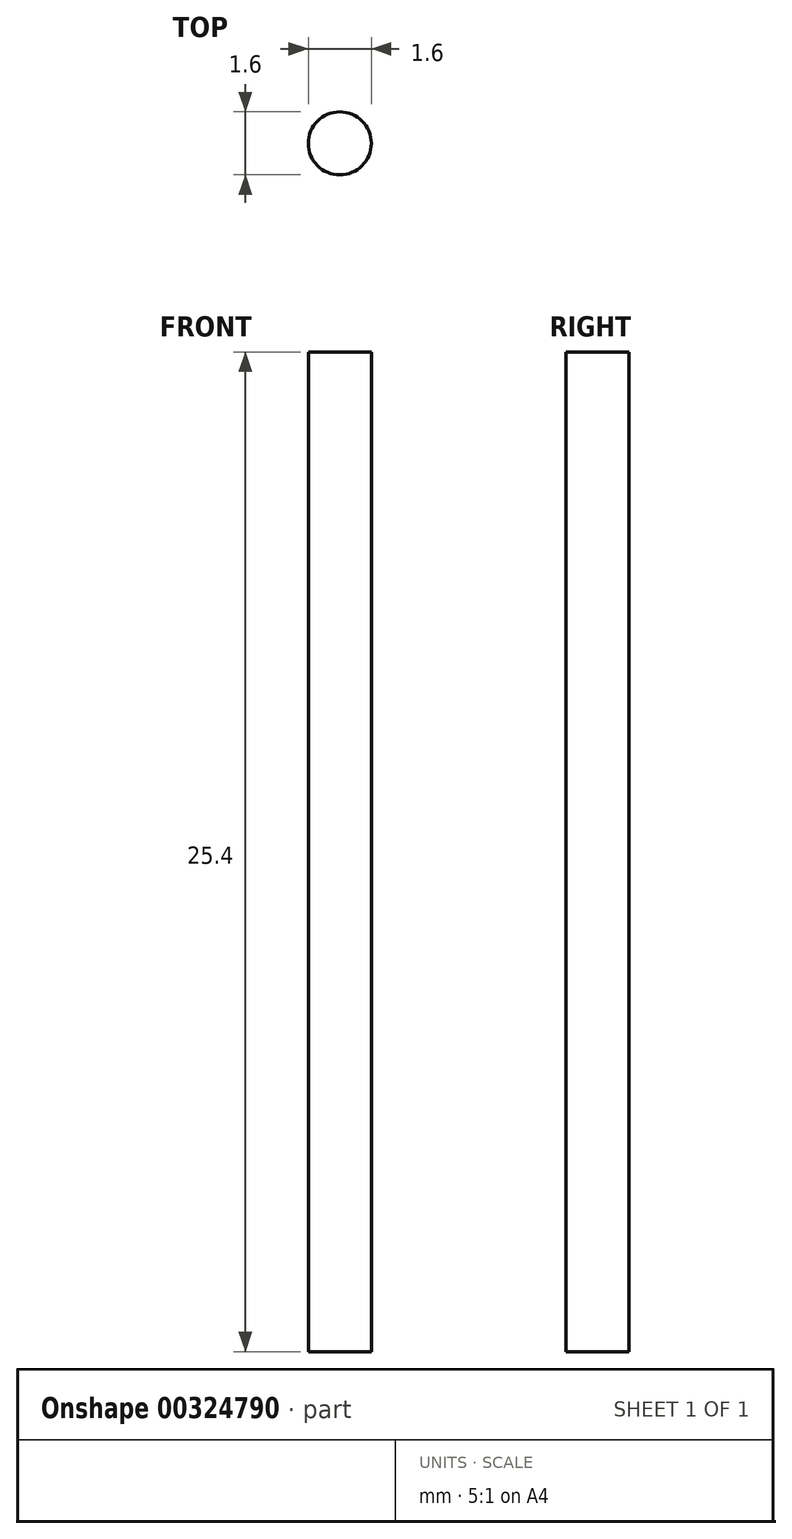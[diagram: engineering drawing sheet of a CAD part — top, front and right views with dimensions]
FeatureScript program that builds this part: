
annotation { "Feature Type Name" : "Feature", "Feature Type Description" : "" }
export const myFeature = defineFeature(function(context is Context, id is Id, definition is map)
    precondition{}
    {
        {
            var Q0;
            Q0=qCreatedBy(makeId("Top.planeOp"),FACE);
            var sketch = newSketch(context, id + "F0", { "sketchPlane" : qUnion([Q0])});
            skCircle(sketch, "E0", {"center": v(0, 0) * mm, "radius": 0.8 * mm});
            skSolve(sketch);
        }
        {
            var Q0;
            Q0=makeQuery(id+"F0.imprint","IMPRINT",FACE,{"disambiguationData":[TD([[makeQuery(id+"F0.imprint","IMPRINT",EDGE,{"derivedFrom":sQuery(id+"F0.wireOp",EDGE,"E0")}),1.0]])]});
            extrude(context, id + "F1", {"entities" : qUnion([Q0]), "depth" : 25.4 * mm, "offsetDistance" : 25.4 * mm});
        }
    });
